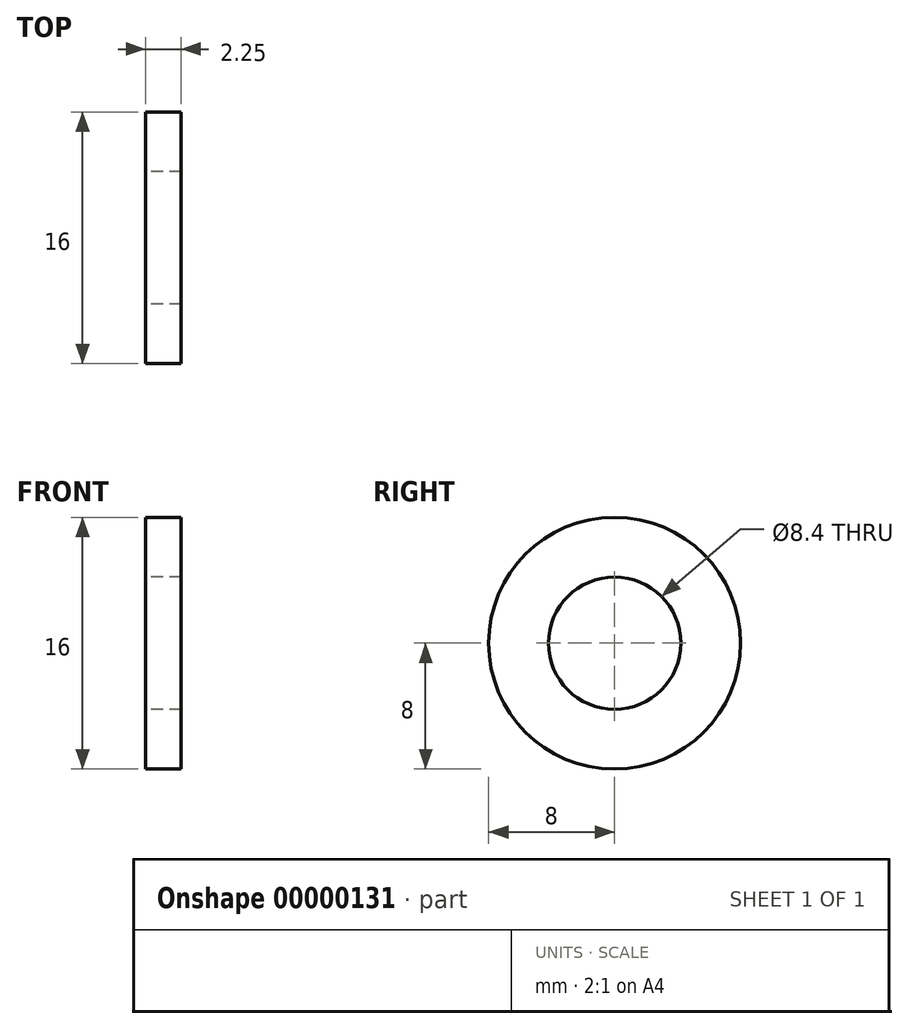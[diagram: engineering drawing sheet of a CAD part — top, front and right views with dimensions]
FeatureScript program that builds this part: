
annotation { "Feature Type Name" : "Feature", "Feature Type Description" : "" }
export const myFeature = defineFeature(function(context is Context, id is Id, definition is map)
    precondition{}
    {
        {
            var Q0;
            Q0=qCreatedBy(makeId("Right.planeOp"),FACE);
            var sketch = newSketch(context, id + "F0", { "sketchPlane" : qUnion([Q0])});
            skCircle(sketch, "E0", {"center": v(0, 0) * mm, "radius": 8 * mm});
            skCircle(sketch, "E1", {"center": v(0, 0) * mm, "radius": 4.2 * mm});
            skSolve(sketch);
        }
        {
            var Q0;
            Q0=makeQuery(id+"F0.imprint","IMPRINT",FACE,{"disambiguationData":[TD([[makeQuery(id+"F0.imprint","IMPRINT",EDGE,{"derivedFrom":sQuery(id+"F0.wireOp",EDGE,"E0")}),1.0]])]});
            extrude(context, id + "F1", {"entities" : qUnion([Q0]), "depth" : 2.25 * mm});
        }
    });
